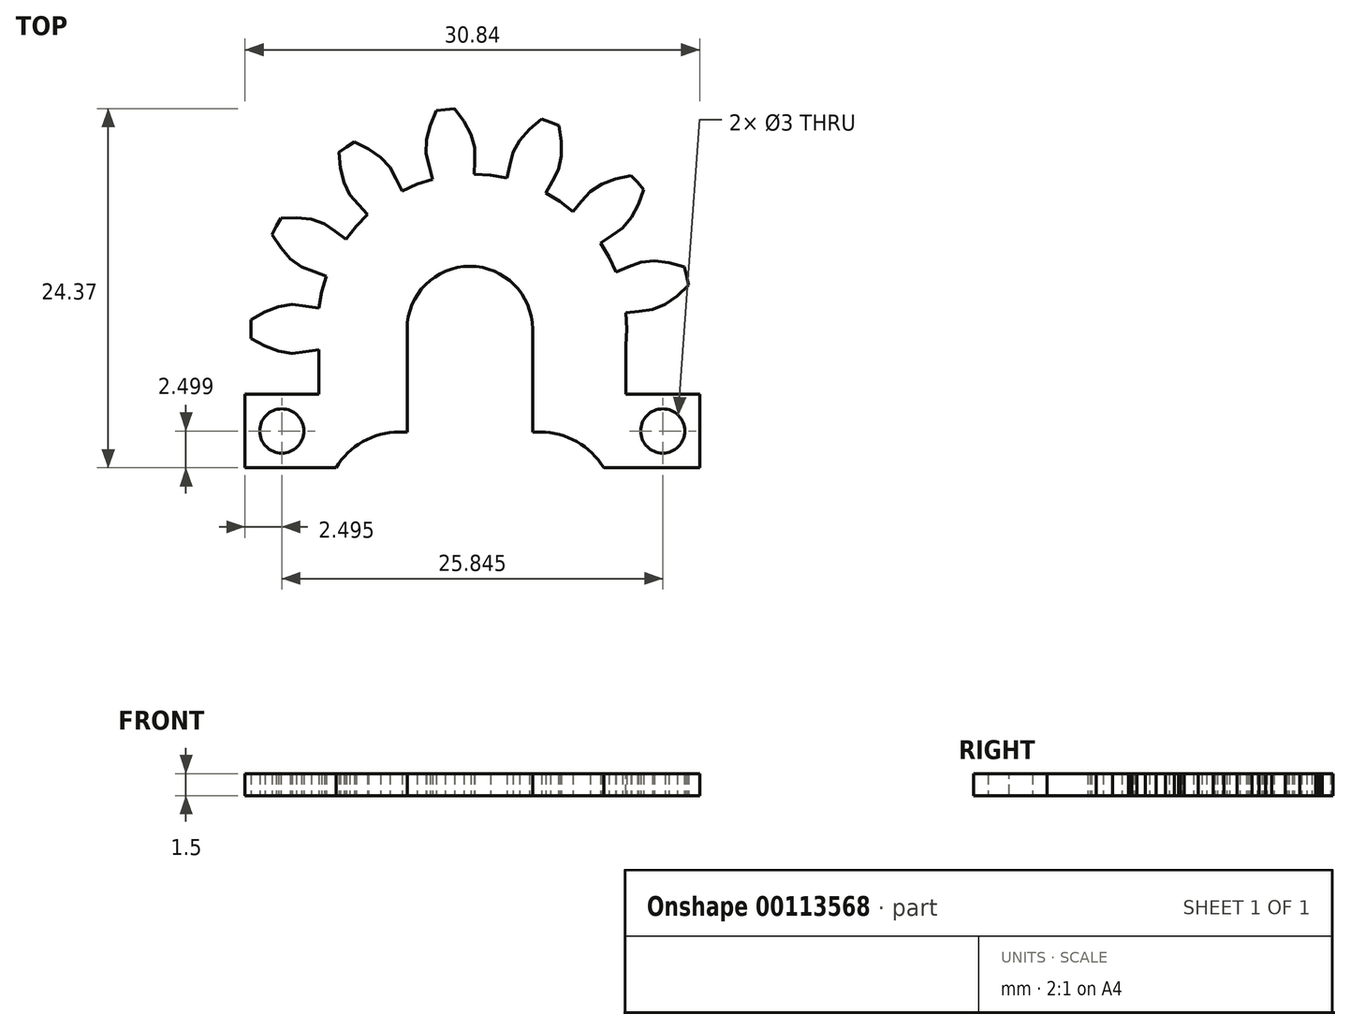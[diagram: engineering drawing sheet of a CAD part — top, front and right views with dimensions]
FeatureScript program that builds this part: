
annotation { "Feature Type Name" : "Feature", "Feature Type Description" : "" }
export const myFeature = defineFeature(function(context is Context, id is Id, definition is map)
    precondition{}
    {
        {
            var Q0;
            Q0=qCreatedBy(makeId("Top.planeOp"),FACE);
            var sketch = newSketch(context, id + "F0", { "sketchPlane" : qUnion([Q0])});
            skLineSegment(sketch, "E0", {"start": v(10.65, 0) * mm, "end": v(10.59, 1.11) * mm});
            skLineSegment(sketch, "E1", {"start": v(10.59, 1.11) * mm, "end": v(11.48, 1.2) * mm});
            skLineSegment(sketch, "E2", {"start": v(11.48, 1.2) * mm, "end": v(12.38, 1.3) * mm});
            skLineSegment(sketch, "E3", {"start": v(12.38, 1.3) * mm, "end": v(13.24, 1.67) * mm});
            skLineSegment(sketch, "E4", {"start": v(13.24, 1.67) * mm, "end": v(14.07, 2.24) * mm});
            skLineSegment(sketch, "E5", {"start": v(14.07, 2.24) * mm, "end": v(14.85, 2.97) * mm});
            skLineSegment(sketch, "E6", {"start": v(14.85, 2.97) * mm, "end": v(14.71, 3.59) * mm});
            skLineSegment(sketch, "E7", {"start": v(14.71, 3.59) * mm, "end": v(14.55, 4.2) * mm});
            skLineSegment(sketch, "E8", {"start": v(14.55, 4.2) * mm, "end": v(13.52, 4.49) * mm});
            skLineSegment(sketch, "E9", {"start": v(13.52, 4.49) * mm, "end": v(12.52, 4.6) * mm});
            skLineSegment(sketch, "E10", {"start": v(12.52, 4.6) * mm, "end": v(11.59, 4.53) * mm});
            skLineSegment(sketch, "E11", {"start": v(11.59, 4.53) * mm, "end": v(10.75, 4.2) * mm});
            skLineSegment(sketch, "E12", {"start": v(10.75, 4.2) * mm, "end": v(9.9, 3.87) * mm});
            skLineSegment(sketch, "E13", {"start": v(9.9, 3.87) * mm, "end": v(9.45, 4.88) * mm});
            skLineSegment(sketch, "E14", {"start": v(9.45, 4.88) * mm, "end": v(8.88, 5.84) * mm});
            skLineSegment(sketch, "E15", {"start": v(8.88, 5.84) * mm, "end": v(9.63, 6.34) * mm});
            skLineSegment(sketch, "E16", {"start": v(9.63, 6.34) * mm, "end": v(10.37, 6.84) * mm});
            skLineSegment(sketch, "E17", {"start": v(10.37, 6.84) * mm, "end": v(10.97, 7.56) * mm});
            skLineSegment(sketch, "E18", {"start": v(10.97, 7.56) * mm, "end": v(11.43, 8.45) * mm});
            skLineSegment(sketch, "E19", {"start": v(11.43, 8.45) * mm, "end": v(11.79, 9.46) * mm});
            skLineSegment(sketch, "E20", {"start": v(11.79, 9.46) * mm, "end": v(11.38, 9.95) * mm});
            skLineSegment(sketch, "E21", {"start": v(11.38, 9.95) * mm, "end": v(10.95, 10.41) * mm});
            skLineSegment(sketch, "E22", {"start": v(10.95, 10.41) * mm, "end": v(9.9, 10.19) * mm});
            skLineSegment(sketch, "E23", {"start": v(9.9, 10.19) * mm, "end": v(8.96, 9.83) * mm});
            skLineSegment(sketch, "E24", {"start": v(8.96, 9.83) * mm, "end": v(8.17, 9.32) * mm});
            skLineSegment(sketch, "E25", {"start": v(8.17, 9.32) * mm, "end": v(7.58, 8.64) * mm});
            skLineSegment(sketch, "E26", {"start": v(7.58, 8.64) * mm, "end": v(7, 7.96) * mm});
            skLineSegment(sketch, "E27", {"start": v(7, 7.96) * mm, "end": v(6.11, 8.64) * mm});
            skLineSegment(sketch, "E28", {"start": v(6.11, 8.64) * mm, "end": v(5.17, 9.22) * mm});
            skLineSegment(sketch, "E29", {"start": v(5.17, 9.22) * mm, "end": v(5.6, 10.01) * mm});
            skLineSegment(sketch, "E30", {"start": v(5.6, 10.01) * mm, "end": v(6.02, 10.8) * mm});
            skLineSegment(sketch, "E31", {"start": v(6.02, 10.8) * mm, "end": v(6.21, 11.72) * mm});
            skLineSegment(sketch, "E32", {"start": v(6.21, 11.72) * mm, "end": v(6.21, 12.73) * mm});
            skLineSegment(sketch, "E33", {"start": v(6.21, 12.73) * mm, "end": v(6.06, 13.79) * mm});
            skLineSegment(sketch, "E34", {"start": v(6.06, 13.79) * mm, "end": v(5.47, 14.03) * mm});
            skLineSegment(sketch, "E35", {"start": v(5.47, 14.03) * mm, "end": v(4.87, 14.24) * mm});
            skLineSegment(sketch, "E36", {"start": v(4.87, 14.24) * mm, "end": v(4.05, 13.55) * mm});
            skLineSegment(sketch, "E37", {"start": v(4.05, 13.55) * mm, "end": v(3.38, 12.8) * mm});
            skLineSegment(sketch, "E38", {"start": v(3.38, 12.8) * mm, "end": v(2.92, 11.98) * mm});
            skLineSegment(sketch, "E39", {"start": v(2.92, 11.98) * mm, "end": v(2.71, 11.1) * mm});
            skLineSegment(sketch, "E40", {"start": v(2.71, 11.1) * mm, "end": v(2.5, 10.23) * mm});
            skLineSegment(sketch, "E41", {"start": v(2.5, 10.23) * mm, "end": v(1.41, 10.42) * mm});
            skLineSegment(sketch, "E42", {"start": v(1.41, 10.42) * mm, "end": v(0.3, 10.5) * mm});
            skLineSegment(sketch, "E43", {"start": v(0.3, 10.5) * mm, "end": v(0.32, 11.4) * mm});
            skLineSegment(sketch, "E44", {"start": v(0.32, 11.4) * mm, "end": v(0.33, 12.3) * mm});
            skLineSegment(sketch, "E45", {"start": v(0.33, 12.3) * mm, "end": v(0.07, 13.2) * mm});
            skLineSegment(sketch, "E46", {"start": v(0.07, 13.2) * mm, "end": v(-0.4, 14.09) * mm});
            skLineSegment(sketch, "E47", {"start": v(-0.4, 14.09) * mm, "end": v(-1.03, 14.95) * mm});
            skLineSegment(sketch, "E48", {"start": v(-1.03, 14.95) * mm, "end": v(-1.66, 14.9) * mm});
            skLineSegment(sketch, "E49", {"start": v(-1.66, 14.9) * mm, "end": v(-2.29, 14.8) * mm});
            skLineSegment(sketch, "E50", {"start": v(-2.29, 14.8) * mm, "end": v(-2.7, 13.81) * mm});
            skLineSegment(sketch, "E51", {"start": v(-2.7, 13.81) * mm, "end": v(-2.93, 12.83) * mm});
            skLineSegment(sketch, "E52", {"start": v(-2.93, 12.83) * mm, "end": v(-2.97, 11.9) * mm});
            skLineSegment(sketch, "E53", {"start": v(-2.97, 11.9) * mm, "end": v(-2.74, 11.03) * mm});
            skLineSegment(sketch, "E54", {"start": v(-2.74, 11.03) * mm, "end": v(-2.52, 10.16) * mm});
            skLineSegment(sketch, "E55", {"start": v(-2.52, 10.16) * mm, "end": v(-3.57, 9.82) * mm});
            skLineSegment(sketch, "E56", {"start": v(-3.57, 9.82) * mm, "end": v(-4.6, 9.37) * mm});
            skLineSegment(sketch, "E57", {"start": v(-4.6, 9.37) * mm, "end": v(-5, 10.17) * mm});
            skLineSegment(sketch, "E58", {"start": v(-5, 10.17) * mm, "end": v(-5.41, 10.97) * mm});
            skLineSegment(sketch, "E59", {"start": v(-5.41, 10.97) * mm, "end": v(-6.05, 11.65) * mm});
            skLineSegment(sketch, "E60", {"start": v(-6.05, 11.65) * mm, "end": v(-6.88, 12.22) * mm});
            skLineSegment(sketch, "E61", {"start": v(-6.88, 12.22) * mm, "end": v(-7.84, 12.7) * mm});
            skLineSegment(sketch, "E62", {"start": v(-7.84, 12.7) * mm, "end": v(-8.37, 12.34) * mm});
            skLineSegment(sketch, "E63", {"start": v(-8.37, 12.34) * mm, "end": v(-8.89, 11.97) * mm});
            skLineSegment(sketch, "E64", {"start": v(-8.89, 11.97) * mm, "end": v(-8.79, 10.9) * mm});
            skLineSegment(sketch, "E65", {"start": v(-8.79, 10.9) * mm, "end": v(-8.55, 9.93) * mm});
            skLineSegment(sketch, "E66", {"start": v(-8.55, 9.93) * mm, "end": v(-8.14, 9.09) * mm});
            skLineSegment(sketch, "E67", {"start": v(-8.14, 9.09) * mm, "end": v(-7.54, 8.42) * mm});
            skLineSegment(sketch, "E68", {"start": v(-7.54, 8.42) * mm, "end": v(-6.93, 7.75) * mm});
            skLineSegment(sketch, "E69", {"start": v(-6.93, 7.75) * mm, "end": v(-7.71, 6.96) * mm});
            skLineSegment(sketch, "E70", {"start": v(-7.71, 6.96) * mm, "end": v(-8.4, 6.1) * mm});
            skLineSegment(sketch, "E71", {"start": v(-8.4, 6.1) * mm, "end": v(-9.14, 6.62) * mm});
            skLineSegment(sketch, "E72", {"start": v(-9.14, 6.62) * mm, "end": v(-9.87, 7.13) * mm});
            skLineSegment(sketch, "E73", {"start": v(-9.87, 7.13) * mm, "end": v(-10.76, 7.43) * mm});
            skLineSegment(sketch, "E74", {"start": v(-10.76, 7.43) * mm, "end": v(-11.76, 7.56) * mm});
            skLineSegment(sketch, "E75", {"start": v(-11.76, 7.56) * mm, "end": v(-12.83, 7.53) * mm});
            skLineSegment(sketch, "E76", {"start": v(-12.83, 7.53) * mm, "end": v(-13.13, 6.97) * mm});
            skLineSegment(sketch, "E77", {"start": v(-13.13, 6.97) * mm, "end": v(-13.42, 6.4) * mm});
            skLineSegment(sketch, "E78", {"start": v(-13.42, 6.4) * mm, "end": v(-12.83, 5.5) * mm});
            skLineSegment(sketch, "E79", {"start": v(-12.83, 5.5) * mm, "end": v(-12.17, 4.75) * mm});
            skLineSegment(sketch, "E80", {"start": v(-12.17, 4.75) * mm, "end": v(-11.41, 4.2) * mm});
            skLineSegment(sketch, "E81", {"start": v(-11.41, 4.2) * mm, "end": v(-10.57, 3.88) * mm});
            skLineSegment(sketch, "E82", {"start": v(-10.57, 3.88) * mm, "end": v(-9.72, 3.58) * mm});
            skLineSegment(sketch, "E83", {"start": v(-9.72, 3.58) * mm, "end": v(-10.05, 2.51) * mm});
            skLineSegment(sketch, "E84", {"start": v(-10.05, 2.51) * mm, "end": v(-10.25, 1.42) * mm});
            skLineSegment(sketch, "E85", {"start": v(-10.25, 1.42) * mm, "end": v(-11.15, 1.54) * mm});
            skLineSegment(sketch, "E86", {"start": v(-11.15, 1.54) * mm, "end": v(-12.04, 1.66) * mm});
            skLineSegment(sketch, "E87", {"start": v(-12.04, 1.66) * mm, "end": v(-12.96, 1.51) * mm});
            skLineSegment(sketch, "E88", {"start": v(-12.96, 1.51) * mm, "end": v(-13.9, 1.16) * mm});
            skLineSegment(sketch, "E89", {"start": v(-13.9, 1.16) * mm, "end": v(-14.84, 0.63) * mm});
            skLineSegment(sketch, "E90", {"start": v(-14.84, 0.63) * mm, "end": v(-14.85, 0) * mm});
            skLineSegment(sketch, "E91", {"start": v(-14.85, 0) * mm, "end": v(-14.84, -0.63) * mm});
            skLineSegment(sketch, "E92", {"start": v(-14.84, -0.63) * mm, "end": v(-13.9, -1.16) * mm});
            skLineSegment(sketch, "E93", {"start": v(-13.9, -1.16) * mm, "end": v(-12.96, -1.51) * mm});
            skLineSegment(sketch, "E94", {"start": v(-12.96, -1.51) * mm, "end": v(-12.04, -1.66) * mm});
            skLineSegment(sketch, "E95", {"start": v(-12.04, -1.66) * mm, "end": v(-11.15, -1.54) * mm});
            skLineSegment(sketch, "E96", {"start": v(-11.15, -1.54) * mm, "end": v(-10.25, -1.42) * mm});
            skLineSegment(sketch, "E97", {"start": v(-10.25, -1.42) * mm, "end": v(-10.05, -2.51) * mm});
            skLineSegment(sketch, "E98", {"start": v(-10.05, -2.51) * mm, "end": v(-9.72, -3.58) * mm});
            skLineSegment(sketch, "E99", {"start": v(-9.72, -3.58) * mm, "end": v(-10.57, -3.88) * mm});
            skLineSegment(sketch, "E100", {"start": v(-10.57, -3.88) * mm, "end": v(-11.41, -4.2) * mm});
            skLineSegment(sketch, "E101", {"start": v(-11.41, -4.2) * mm, "end": v(-12.17, -4.75) * mm});
            skLineSegment(sketch, "E102", {"start": v(-12.17, -4.75) * mm, "end": v(-12.83, -5.5) * mm});
            skLineSegment(sketch, "E103", {"start": v(-12.83, -5.5) * mm, "end": v(-13.42, -6.4) * mm});
            skLineSegment(sketch, "E104", {"start": v(-13.42, -6.4) * mm, "end": v(-13.13, -6.97) * mm});
            skLineSegment(sketch, "E105", {"start": v(-13.13, -6.97) * mm, "end": v(-12.83, -7.53) * mm});
            skLineSegment(sketch, "E106", {"start": v(-12.83, -7.53) * mm, "end": v(-11.76, -7.56) * mm});
            skLineSegment(sketch, "E107", {"start": v(-11.76, -7.56) * mm, "end": v(-10.76, -7.43) * mm});
            skLineSegment(sketch, "E108", {"start": v(-10.76, -7.43) * mm, "end": v(-9.87, -7.13) * mm});
            skLineSegment(sketch, "E109", {"start": v(-9.87, -7.13) * mm, "end": v(-9.14, -6.62) * mm});
            skLineSegment(sketch, "E110", {"start": v(-9.14, -6.62) * mm, "end": v(-8.4, -6.1) * mm});
            skLineSegment(sketch, "E111", {"start": v(-8.4, -6.1) * mm, "end": v(-7.71, -6.96) * mm});
            skLineSegment(sketch, "E112", {"start": v(-7.71, -6.96) * mm, "end": v(-6.93, -7.75) * mm});
            skLineSegment(sketch, "E113", {"start": v(-6.93, -7.75) * mm, "end": v(-7.54, -8.42) * mm});
            skLineSegment(sketch, "E114", {"start": v(-7.54, -8.42) * mm, "end": v(-8.14, -9.09) * mm});
            skLineSegment(sketch, "E115", {"start": v(-8.14, -9.09) * mm, "end": v(-8.55, -9.93) * mm});
            skLineSegment(sketch, "E116", {"start": v(-8.55, -9.93) * mm, "end": v(-8.79, -10.9) * mm});
            skLineSegment(sketch, "E117", {"start": v(-8.79, -10.9) * mm, "end": v(-8.89, -11.97) * mm});
            skLineSegment(sketch, "E118", {"start": v(-8.89, -11.97) * mm, "end": v(-8.37, -12.34) * mm});
            skLineSegment(sketch, "E119", {"start": v(-8.37, -12.34) * mm, "end": v(-7.84, -12.7) * mm});
            skLineSegment(sketch, "E120", {"start": v(-7.84, -12.7) * mm, "end": v(-6.88, -12.22) * mm});
            skLineSegment(sketch, "E121", {"start": v(-6.88, -12.22) * mm, "end": v(-6.05, -11.65) * mm});
            skLineSegment(sketch, "E122", {"start": v(-6.05, -11.65) * mm, "end": v(-5.41, -10.97) * mm});
            skLineSegment(sketch, "E123", {"start": v(-5.41, -10.97) * mm, "end": v(-5, -10.17) * mm});
            skLineSegment(sketch, "E124", {"start": v(-5, -10.17) * mm, "end": v(-4.6, -9.37) * mm});
            skLineSegment(sketch, "E125", {"start": v(-4.6, -9.37) * mm, "end": v(-3.57, -9.82) * mm});
            skLineSegment(sketch, "E126", {"start": v(-3.57, -9.82) * mm, "end": v(-2.52, -10.16) * mm});
            skLineSegment(sketch, "E127", {"start": v(-2.52, -10.16) * mm, "end": v(-2.74, -11.03) * mm});
            skLineSegment(sketch, "E128", {"start": v(-2.74, -11.03) * mm, "end": v(-2.97, -11.9) * mm});
            skLineSegment(sketch, "E129", {"start": v(-2.97, -11.9) * mm, "end": v(-2.93, -12.83) * mm});
            skLineSegment(sketch, "E130", {"start": v(-2.93, -12.83) * mm, "end": v(-2.7, -13.81) * mm});
            skLineSegment(sketch, "E131", {"start": v(-2.7, -13.81) * mm, "end": v(-2.29, -14.8) * mm});
            skLineSegment(sketch, "E132", {"start": v(-2.29, -14.8) * mm, "end": v(-1.66, -14.9) * mm});
            skLineSegment(sketch, "E133", {"start": v(-1.66, -14.9) * mm, "end": v(-1.03, -14.95) * mm});
            skLineSegment(sketch, "E134", {"start": v(-1.03, -14.95) * mm, "end": v(-0.4, -14.09) * mm});
            skLineSegment(sketch, "E135", {"start": v(-0.4, -14.09) * mm, "end": v(0.07, -13.2) * mm});
            skLineSegment(sketch, "E136", {"start": v(0.07, -13.2) * mm, "end": v(0.33, -12.3) * mm});
            skLineSegment(sketch, "E137", {"start": v(0.33, -12.3) * mm, "end": v(0.32, -11.4) * mm});
            skLineSegment(sketch, "E138", {"start": v(0.32, -11.4) * mm, "end": v(0.3, -10.5) * mm});
            skLineSegment(sketch, "E139", {"start": v(0.3, -10.5) * mm, "end": v(1.41, -10.42) * mm});
            skLineSegment(sketch, "E140", {"start": v(1.41, -10.42) * mm, "end": v(2.5, -10.23) * mm});
            skLineSegment(sketch, "E141", {"start": v(2.5, -10.23) * mm, "end": v(2.71, -11.1) * mm});
            skLineSegment(sketch, "E142", {"start": v(2.71, -11.1) * mm, "end": v(2.92, -11.98) * mm});
            skLineSegment(sketch, "E143", {"start": v(2.92, -11.98) * mm, "end": v(3.38, -12.8) * mm});
            skLineSegment(sketch, "E144", {"start": v(3.38, -12.8) * mm, "end": v(4.05, -13.55) * mm});
            skLineSegment(sketch, "E145", {"start": v(4.05, -13.55) * mm, "end": v(4.87, -14.24) * mm});
            skLineSegment(sketch, "E146", {"start": v(4.87, -14.24) * mm, "end": v(5.47, -14.03) * mm});
            skLineSegment(sketch, "E147", {"start": v(5.47, -14.03) * mm, "end": v(6.06, -13.79) * mm});
            skLineSegment(sketch, "E148", {"start": v(6.06, -13.79) * mm, "end": v(6.21, -12.73) * mm});
            skLineSegment(sketch, "E149", {"start": v(6.21, -12.73) * mm, "end": v(6.21, -11.72) * mm});
            skLineSegment(sketch, "E150", {"start": v(6.21, -11.72) * mm, "end": v(6.02, -10.8) * mm});
            skLineSegment(sketch, "E151", {"start": v(6.02, -10.8) * mm, "end": v(5.6, -10.01) * mm});
            skLineSegment(sketch, "E152", {"start": v(5.6, -10.01) * mm, "end": v(5.17, -9.22) * mm});
            skLineSegment(sketch, "E153", {"start": v(5.17, -9.22) * mm, "end": v(6.11, -8.64) * mm});
            skLineSegment(sketch, "E154", {"start": v(6.11, -8.64) * mm, "end": v(7, -7.96) * mm});
            skLineSegment(sketch, "E155", {"start": v(7, -7.96) * mm, "end": v(7.58, -8.64) * mm});
            skLineSegment(sketch, "E156", {"start": v(7.58, -8.64) * mm, "end": v(8.17, -9.32) * mm});
            skLineSegment(sketch, "E157", {"start": v(8.17, -9.32) * mm, "end": v(8.96, -9.83) * mm});
            skLineSegment(sketch, "E158", {"start": v(8.96, -9.83) * mm, "end": v(9.9, -10.19) * mm});
            skLineSegment(sketch, "E159", {"start": v(9.9, -10.19) * mm, "end": v(10.95, -10.41) * mm});
            skLineSegment(sketch, "E160", {"start": v(10.95, -10.41) * mm, "end": v(11.38, -9.95) * mm});
            skLineSegment(sketch, "E161", {"start": v(11.38, -9.95) * mm, "end": v(11.79, -9.46) * mm});
            skLineSegment(sketch, "E162", {"start": v(11.79, -9.46) * mm, "end": v(11.43, -8.45) * mm});
            skLineSegment(sketch, "E163", {"start": v(11.43, -8.45) * mm, "end": v(10.97, -7.56) * mm});
            skLineSegment(sketch, "E164", {"start": v(10.97, -7.56) * mm, "end": v(10.37, -6.84) * mm});
            skLineSegment(sketch, "E165", {"start": v(10.37, -6.84) * mm, "end": v(9.63, -6.34) * mm});
            skLineSegment(sketch, "E166", {"start": v(9.63, -6.34) * mm, "end": v(8.88, -5.84) * mm});
            skLineSegment(sketch, "E167", {"start": v(8.88, -5.84) * mm, "end": v(9.45, -4.88) * mm});
            skLineSegment(sketch, "E168", {"start": v(9.45, -4.88) * mm, "end": v(9.9, -3.87) * mm});
            skLineSegment(sketch, "E169", {"start": v(9.9, -3.87) * mm, "end": v(10.75, -4.2) * mm});
            skLineSegment(sketch, "E170", {"start": v(10.75, -4.2) * mm, "end": v(11.59, -4.53) * mm});
            skLineSegment(sketch, "E171", {"start": v(11.59, -4.53) * mm, "end": v(12.52, -4.6) * mm});
            skLineSegment(sketch, "E172", {"start": v(12.52, -4.6) * mm, "end": v(13.52, -4.49) * mm});
            skLineSegment(sketch, "E173", {"start": v(13.52, -4.49) * mm, "end": v(14.55, -4.2) * mm});
            skLineSegment(sketch, "E174", {"start": v(14.55, -4.2) * mm, "end": v(14.71, -3.59) * mm});
            skLineSegment(sketch, "E175", {"start": v(14.71, -3.59) * mm, "end": v(14.85, -2.97) * mm});
            skLineSegment(sketch, "E176", {"start": v(14.85, -2.97) * mm, "end": v(14.07, -2.24) * mm});
            skLineSegment(sketch, "E177", {"start": v(14.07, -2.24) * mm, "end": v(13.24, -1.67) * mm});
            skLineSegment(sketch, "E178", {"start": v(13.24, -1.67) * mm, "end": v(12.38, -1.3) * mm});
            skLineSegment(sketch, "E179", {"start": v(12.38, -1.3) * mm, "end": v(11.48, -1.2) * mm});
            skLineSegment(sketch, "E180", {"start": v(11.48, -1.2) * mm, "end": v(10.59, -1.11) * mm});
            skLineSegment(sketch, "E181", {"start": v(10.65, 0) * mm, "end": v(10.59, -1.11) * mm});
            skSolve(sketch);
        }
        {
            var Q0;
            Q0 = qSketchRegion(id + "F0", true);
            extrude(context, id + "F1", {"entities" : qUnion([Q0]), "depth" : 1.5 * mm});
        }
        {
            var Q0;
            Q0=makeQuery(id+"F1.opExtrude","CAP_FACE",FACE,{"disambiguationData":[OSD([sQuery(id+"F0.wireOp",EDGE,"E0"),sQuery(id+"F0.wireOp",EDGE,"E1"),sQuery(id+"F0.wireOp",EDGE,"E2"),sQuery(id+"F0.wireOp",EDGE,"E3"),sQuery(id+"F0.wireOp",EDGE,"E4"),sQuery(id+"F0.wireOp",EDGE,"E5"),sQuery(id+"F0.wireOp",EDGE,"E6"),sQuery(id+"F0.wireOp",EDGE,"E7"),sQuery(id+"F0.wireOp",EDGE,"E8"),sQuery(id+"F0.wireOp",EDGE,"E9"),sQuery(id+"F0.wireOp",EDGE,"E10"),sQuery(id+"F0.wireOp",EDGE,"E11"),sQuery(id+"F0.wireOp",EDGE,"E12"),sQuery(id+"F0.wireOp",EDGE,"E13"),sQuery(id+"F0.wireOp",EDGE,"E14"),sQuery(id+"F0.wireOp",EDGE,"E15"),sQuery(id+"F0.wireOp",EDGE,"E16"),sQuery(id+"F0.wireOp",EDGE,"E17"),sQuery(id+"F0.wireOp",EDGE,"E18"),sQuery(id+"F0.wireOp",EDGE,"E19"),sQuery(id+"F0.wireOp",EDGE,"E20"),sQuery(id+"F0.wireOp",EDGE,"E21"),sQuery(id+"F0.wireOp",EDGE,"E22"),sQuery(id+"F0.wireOp",EDGE,"E23"),sQuery(id+"F0.wireOp",EDGE,"E24"),sQuery(id+"F0.wireOp",EDGE,"E25"),sQuery(id+"F0.wireOp",EDGE,"E26"),sQuery(id+"F0.wireOp",EDGE,"E27"),sQuery(id+"F0.wireOp",EDGE,"E28"),sQuery(id+"F0.wireOp",EDGE,"E29"),sQuery(id+"F0.wireOp",EDGE,"E30"),sQuery(id+"F0.wireOp",EDGE,"E31"),sQuery(id+"F0.wireOp",EDGE,"E32"),sQuery(id+"F0.wireOp",EDGE,"E33"),sQuery(id+"F0.wireOp",EDGE,"E34"),sQuery(id+"F0.wireOp",EDGE,"E35"),sQuery(id+"F0.wireOp",EDGE,"E36"),sQuery(id+"F0.wireOp",EDGE,"E37"),sQuery(id+"F0.wireOp",EDGE,"E38"),sQuery(id+"F0.wireOp",EDGE,"E39"),sQuery(id+"F0.wireOp",EDGE,"E40"),sQuery(id+"F0.wireOp",EDGE,"E41"),sQuery(id+"F0.wireOp",EDGE,"E42"),sQuery(id+"F0.wireOp",EDGE,"E43"),sQuery(id+"F0.wireOp",EDGE,"E44"),sQuery(id+"F0.wireOp",EDGE,"E45"),sQuery(id+"F0.wireOp",EDGE,"E46"),sQuery(id+"F0.wireOp",EDGE,"E47"),sQuery(id+"F0.wireOp",EDGE,"E48"),sQuery(id+"F0.wireOp",EDGE,"E49"),sQuery(id+"F0.wireOp",EDGE,"E50"),sQuery(id+"F0.wireOp",EDGE,"E51"),sQuery(id+"F0.wireOp",EDGE,"E52"),sQuery(id+"F0.wireOp",EDGE,"E53"),sQuery(id+"F0.wireOp",EDGE,"E54"),sQuery(id+"F0.wireOp",EDGE,"E55"),sQuery(id+"F0.wireOp",EDGE,"E56"),sQuery(id+"F0.wireOp",EDGE,"E57"),sQuery(id+"F0.wireOp",EDGE,"E58"),sQuery(id+"F0.wireOp",EDGE,"E59"),sQuery(id+"F0.wireOp",EDGE,"E60"),sQuery(id+"F0.wireOp",EDGE,"E61"),sQuery(id+"F0.wireOp",EDGE,"E62"),sQuery(id+"F0.wireOp",EDGE,"E63"),sQuery(id+"F0.wireOp",EDGE,"E64"),sQuery(id+"F0.wireOp",EDGE,"E65"),sQuery(id+"F0.wireOp",EDGE,"E66"),sQuery(id+"F0.wireOp",EDGE,"E67"),sQuery(id+"F0.wireOp",EDGE,"E68"),sQuery(id+"F0.wireOp",EDGE,"E69"),sQuery(id+"F0.wireOp",EDGE,"E70"),sQuery(id+"F0.wireOp",EDGE,"E71"),sQuery(id+"F0.wireOp",EDGE,"E72"),sQuery(id+"F0.wireOp",EDGE,"E73"),sQuery(id+"F0.wireOp",EDGE,"E74"),sQuery(id+"F0.wireOp",EDGE,"E75"),sQuery(id+"F0.wireOp",EDGE,"E76"),sQuery(id+"F0.wireOp",EDGE,"E77"),sQuery(id+"F0.wireOp",EDGE,"E78"),sQuery(id+"F0.wireOp",EDGE,"E79"),sQuery(id+"F0.wireOp",EDGE,"E80"),sQuery(id+"F0.wireOp",EDGE,"E81"),sQuery(id+"F0.wireOp",EDGE,"E82"),sQuery(id+"F0.wireOp",EDGE,"E83"),sQuery(id+"F0.wireOp",EDGE,"E84"),sQuery(id+"F0.wireOp",EDGE,"E85"),sQuery(id+"F0.wireOp",EDGE,"E86"),sQuery(id+"F0.wireOp",EDGE,"E87"),sQuery(id+"F0.wireOp",EDGE,"E88"),sQuery(id+"F0.wireOp",EDGE,"E89"),sQuery(id+"F0.wireOp",EDGE,"E90"),sQuery(id+"F0.wireOp",EDGE,"E91"),sQuery(id+"F0.wireOp",EDGE,"E92"),sQuery(id+"F0.wireOp",EDGE,"E93"),sQuery(id+"F0.wireOp",EDGE,"E94"),sQuery(id+"F0.wireOp",EDGE,"E95"),sQuery(id+"F0.wireOp",EDGE,"E96"),sQuery(id+"F0.wireOp",EDGE,"E97"),sQuery(id+"F0.wireOp",EDGE,"E98"),sQuery(id+"F0.wireOp",EDGE,"E99"),sQuery(id+"F0.wireOp",EDGE,"E100"),sQuery(id+"F0.wireOp",EDGE,"E101"),sQuery(id+"F0.wireOp",EDGE,"E102"),sQuery(id+"F0.wireOp",EDGE,"E103"),sQuery(id+"F0.wireOp",EDGE,"E104"),sQuery(id+"F0.wireOp",EDGE,"E105"),sQuery(id+"F0.wireOp",EDGE,"E106"),sQuery(id+"F0.wireOp",EDGE,"E107"),sQuery(id+"F0.wireOp",EDGE,"E108"),sQuery(id+"F0.wireOp",EDGE,"E109"),sQuery(id+"F0.wireOp",EDGE,"E110"),sQuery(id+"F0.wireOp",EDGE,"E111"),sQuery(id+"F0.wireOp",EDGE,"E112"),sQuery(id+"F0.wireOp",EDGE,"E113"),sQuery(id+"F0.wireOp",EDGE,"E114"),sQuery(id+"F0.wireOp",EDGE,"E115"),sQuery(id+"F0.wireOp",EDGE,"E116"),sQuery(id+"F0.wireOp",EDGE,"E117"),sQuery(id+"F0.wireOp",EDGE,"E118"),sQuery(id+"F0.wireOp",EDGE,"E119"),sQuery(id+"F0.wireOp",EDGE,"E120"),sQuery(id+"F0.wireOp",EDGE,"E121"),sQuery(id+"F0.wireOp",EDGE,"E122"),sQuery(id+"F0.wireOp",EDGE,"E123"),sQuery(id+"F0.wireOp",EDGE,"E124"),sQuery(id+"F0.wireOp",EDGE,"E125"),sQuery(id+"F0.wireOp",EDGE,"E126"),sQuery(id+"F0.wireOp",EDGE,"E127"),sQuery(id+"F0.wireOp",EDGE,"E128"),sQuery(id+"F0.wireOp",EDGE,"E129"),sQuery(id+"F0.wireOp",EDGE,"E130"),sQuery(id+"F0.wireOp",EDGE,"E131"),sQuery(id+"F0.wireOp",EDGE,"E132"),sQuery(id+"F0.wireOp",EDGE,"E133"),sQuery(id+"F0.wireOp",EDGE,"E134"),sQuery(id+"F0.wireOp",EDGE,"E135"),sQuery(id+"F0.wireOp",EDGE,"E136"),sQuery(id+"F0.wireOp",EDGE,"E137"),sQuery(id+"F0.wireOp",EDGE,"E138"),sQuery(id+"F0.wireOp",EDGE,"E139"),sQuery(id+"F0.wireOp",EDGE,"E140"),sQuery(id+"F0.wireOp",EDGE,"E141"),sQuery(id+"F0.wireOp",EDGE,"E142"),sQuery(id+"F0.wireOp",EDGE,"E143"),sQuery(id+"F0.wireOp",EDGE,"E144"),sQuery(id+"F0.wireOp",EDGE,"E145"),sQuery(id+"F0.wireOp",EDGE,"E146"),sQuery(id+"F0.wireOp",EDGE,"E147"),sQuery(id+"F0.wireOp",EDGE,"E148"),sQuery(id+"F0.wireOp",EDGE,"E149"),sQuery(id+"F0.wireOp",EDGE,"E150"),sQuery(id+"F0.wireOp",EDGE,"E151"),sQuery(id+"F0.wireOp",EDGE,"E152"),sQuery(id+"F0.wireOp",EDGE,"E153"),sQuery(id+"F0.wireOp",EDGE,"E154"),sQuery(id+"F0.wireOp",EDGE,"E155"),sQuery(id+"F0.wireOp",EDGE,"E156"),sQuery(id+"F0.wireOp",EDGE,"E157"),sQuery(id+"F0.wireOp",EDGE,"E158"),sQuery(id+"F0.wireOp",EDGE,"E159"),sQuery(id+"F0.wireOp",EDGE,"E160"),sQuery(id+"F0.wireOp",EDGE,"E161"),sQuery(id+"F0.wireOp",EDGE,"E162"),sQuery(id+"F0.wireOp",EDGE,"E163"),sQuery(id+"F0.wireOp",EDGE,"E164"),sQuery(id+"F0.wireOp",EDGE,"E165"),sQuery(id+"F0.wireOp",EDGE,"E166"),sQuery(id+"F0.wireOp",EDGE,"E167"),sQuery(id+"F0.wireOp",EDGE,"E168"),sQuery(id+"F0.wireOp",EDGE,"E169"),sQuery(id+"F0.wireOp",EDGE,"E170"),sQuery(id+"F0.wireOp",EDGE,"E171"),sQuery(id+"F0.wireOp",EDGE,"E172"),sQuery(id+"F0.wireOp",EDGE,"E173"),sQuery(id+"F0.wireOp",EDGE,"E174"),sQuery(id+"F0.wireOp",EDGE,"E175"),sQuery(id+"F0.wireOp",EDGE,"E176"),sQuery(id+"F0.wireOp",EDGE,"E177"),sQuery(id+"F0.wireOp",EDGE,"E178"),sQuery(id+"F0.wireOp",EDGE,"E179"),sQuery(id+"F0.wireOp",EDGE,"E180"),sQuery(id+"F0.wireOp",EDGE,"E181")])],"isStart":false});
            var sketch = newSketch(context, id + "F2", { "sketchPlane" : qUnion([Q0])});
            skArc(sketch, "E182", {"start": v(4.25, 0) * mm, "mid": v(0, 4.25) * mm, "end": v(-4.25, 0) * mm});
            skLineSegment(sketch, "E183", {"start": v(-10.25, -1.42) * mm, "end": v(-4.25, -1.42) * mm});
            skLineSegment(sketch, "E184.0", {"start": v(10.65, 0) * mm, "end": v(10.59, -1.11) * mm});
            skLineSegment(sketch, "E185", {"start": v(10.59, -1.11) * mm, "end": v(10.59, -1.42) * mm});
            skLineSegment(sketch, "E186", {"start": v(-4.25, 0) * mm, "end": v(-4.25, -1.42) * mm});
            skLineSegment(sketch, "E187.MirrorCS", {"start": v(4.25, 0) * mm, "end": v(4.25, -1.42) * mm});
            skLineSegment(sketch, "E188.trimOffspring", {"start": v(4.25, -1.42) * mm, "end": v(10.59, -1.42) * mm});
            skSolve(sketch);
        }
        {
            var Q0;
            Q0=makeQuery(id+"F2.imprint","IMPRINT",FACE,{"disambiguationData":[TD([[makeQuery(id+"F2.imprint","IMPRINT",EDGE,{"derivedFrom":sQuery(id+"F2.wireOp",EDGE,"E182")}),1.0]])]});
            extrude(context, id + "F3", {"entities" : qUnion([Q0]), "operationType" : NewBodyOperationType.REMOVE, "endBound" : BoundingType.UP_TO_NEXT, "oppositeDirection" : true, "depth" : 25 * mm});
        }
        {
            var Q0;
            Q0=makeQuery(id+"F3.boolean.opBoolean","COPY",FACE,{"derivedFrom":makeQuery(id+"F3.opExtrude","SWEPT_FACE",FACE,{"disambiguationData":[OSD([sQuery(id+"F2.wireOp",EDGE,"E183")])]})});
            var sketch = newSketch(context, id + "F4", { "sketchPlane" : qUnion([Q0])});
            skLineSegment(sketch, "E189.bottom", {"start": v(-10.25, 1.5) * mm, "end": v(-4.25, 1.5) * mm});
            skLineSegment(sketch, "E189.top", {"start": v(-10.25, 0) * mm, "end": v(-4.25, 0) * mm});
            skLineSegment(sketch, "E189.left", {"start": v(-10.25, 1.5) * mm, "end": v(-10.25, 0) * mm});
            skLineSegment(sketch, "E189.right", {"start": v(-4.25, 1.5) * mm, "end": v(-4.25, 0) * mm});
            skLineSegment(sketch, "E190.0", {"start": v(4.25, 1.5) * mm, "end": v(10.59, 1.5) * mm});
            skLineSegment(sketch, "E191.0", {"start": v(4.25, 0) * mm, "end": v(4.25, 1.5) * mm});
            skLineSegment(sketch, "E192.0.0", {"start": v(10.59, 0) * mm, "end": v(10.59, 1.5) * mm});
            skLineSegment(sketch, "E192.0.1", {"start": v(10.59, 1.5) * mm, "end": v(4.25, 1.5) * mm});
            skLineSegment(sketch, "E192.0.2", {"start": v(4.25, 1.5) * mm, "end": v(4.25, 0) * mm});
            skLineSegment(sketch, "E192.0.3", {"start": v(4.25, 0) * mm, "end": v(10.59, 0) * mm});
            skSolve(sketch);
        }
        {
            var Q0;
            Q0 = qSketchRegion(id + "F4", true);
            extrude(context, id + "F5", {"entities" : qUnion([Q0]), "operationType" : NewBodyOperationType.ADD, "depth" : 8 * mm});
        }
        {
            var Q0;
            Q0=makeQuery(id+"F5.boolean.opBoolean","MERGE",FACE,{"derivedFrom":[makeQuery(id+"F3.boolean.opBoolean","COPY",FACE,{"derivedFrom":makeQuery(id+"F3.opExtrude","SWEPT_FACE",FACE,{"disambiguationData":[OSD([sQuery(id+"F2.wireOp",EDGE,"E185")])]})}),makeQuery(id+"F5.opExtrude","SWEPT_FACE",FACE,{"disambiguationData":[OSD([sQuery(id+"F4.wireOp",EDGE,"E192.0.0")])]})]});
            var sketch = newSketch(context, id + "F6", { "sketchPlane" : qUnion([Q0])});
            skLineSegment(sketch, "E193.bottom", {"start": v(-9.42, 0) * mm, "end": v(-4.42, 0) * mm});
            skLineSegment(sketch, "E193.top", {"start": v(-9.42, 1.5) * mm, "end": v(-4.42, 1.5) * mm});
            skLineSegment(sketch, "E193.left", {"start": v(-9.42, 0) * mm, "end": v(-9.42, 1.5) * mm});
            skLineSegment(sketch, "E193.right", {"start": v(-4.42, 0) * mm, "end": v(-4.42, 1.5) * mm});
            skSolve(sketch);
        }
        {
            var Q0;
            Q0 = qSketchRegion(id + "F6", true);
            extrude(context, id + "F7", {"entities" : qUnion([Q0]), "operationType" : NewBodyOperationType.ADD, "depth" : 5 * mm});
        }
        {
            var Q0;
            Q0=makeQuery(id+"F7.boolean.opBoolean","MERGE",FACE,{"derivedFrom":[makeQuery(id+"F5.boolean.opBoolean","MERGE",FACE,{"derivedFrom":[makeQuery(id+"F1.opExtrude","CAP_FACE",FACE,{"disambiguationData":[OSD([sQuery(id+"F0.wireOp",EDGE,"E0"),sQuery(id+"F0.wireOp",EDGE,"E1"),sQuery(id+"F0.wireOp",EDGE,"E2"),sQuery(id+"F0.wireOp",EDGE,"E3"),sQuery(id+"F0.wireOp",EDGE,"E4"),sQuery(id+"F0.wireOp",EDGE,"E5"),sQuery(id+"F0.wireOp",EDGE,"E6"),sQuery(id+"F0.wireOp",EDGE,"E7"),sQuery(id+"F0.wireOp",EDGE,"E8"),sQuery(id+"F0.wireOp",EDGE,"E9"),sQuery(id+"F0.wireOp",EDGE,"E10"),sQuery(id+"F0.wireOp",EDGE,"E11"),sQuery(id+"F0.wireOp",EDGE,"E12"),sQuery(id+"F0.wireOp",EDGE,"E13"),sQuery(id+"F0.wireOp",EDGE,"E14"),sQuery(id+"F0.wireOp",EDGE,"E15"),sQuery(id+"F0.wireOp",EDGE,"E16"),sQuery(id+"F0.wireOp",EDGE,"E17"),sQuery(id+"F0.wireOp",EDGE,"E18"),sQuery(id+"F0.wireOp",EDGE,"E19"),sQuery(id+"F0.wireOp",EDGE,"E20"),sQuery(id+"F0.wireOp",EDGE,"E21"),sQuery(id+"F0.wireOp",EDGE,"E22"),sQuery(id+"F0.wireOp",EDGE,"E23"),sQuery(id+"F0.wireOp",EDGE,"E24"),sQuery(id+"F0.wireOp",EDGE,"E25"),sQuery(id+"F0.wireOp",EDGE,"E26"),sQuery(id+"F0.wireOp",EDGE,"E27"),sQuery(id+"F0.wireOp",EDGE,"E28"),sQuery(id+"F0.wireOp",EDGE,"E29"),sQuery(id+"F0.wireOp",EDGE,"E30"),sQuery(id+"F0.wireOp",EDGE,"E31"),sQuery(id+"F0.wireOp",EDGE,"E32"),sQuery(id+"F0.wireOp",EDGE,"E33"),sQuery(id+"F0.wireOp",EDGE,"E34"),sQuery(id+"F0.wireOp",EDGE,"E35"),sQuery(id+"F0.wireOp",EDGE,"E36"),sQuery(id+"F0.wireOp",EDGE,"E37"),sQuery(id+"F0.wireOp",EDGE,"E38"),sQuery(id+"F0.wireOp",EDGE,"E39"),sQuery(id+"F0.wireOp",EDGE,"E40"),sQuery(id+"F0.wireOp",EDGE,"E41"),sQuery(id+"F0.wireOp",EDGE,"E42"),sQuery(id+"F0.wireOp",EDGE,"E43"),sQuery(id+"F0.wireOp",EDGE,"E44"),sQuery(id+"F0.wireOp",EDGE,"E45"),sQuery(id+"F0.wireOp",EDGE,"E46"),sQuery(id+"F0.wireOp",EDGE,"E47"),sQuery(id+"F0.wireOp",EDGE,"E48"),sQuery(id+"F0.wireOp",EDGE,"E49"),sQuery(id+"F0.wireOp",EDGE,"E50"),sQuery(id+"F0.wireOp",EDGE,"E51"),sQuery(id+"F0.wireOp",EDGE,"E52"),sQuery(id+"F0.wireOp",EDGE,"E53"),sQuery(id+"F0.wireOp",EDGE,"E54"),sQuery(id+"F0.wireOp",EDGE,"E55"),sQuery(id+"F0.wireOp",EDGE,"E56"),sQuery(id+"F0.wireOp",EDGE,"E57"),sQuery(id+"F0.wireOp",EDGE,"E58"),sQuery(id+"F0.wireOp",EDGE,"E59"),sQuery(id+"F0.wireOp",EDGE,"E60"),sQuery(id+"F0.wireOp",EDGE,"E61"),sQuery(id+"F0.wireOp",EDGE,"E62"),sQuery(id+"F0.wireOp",EDGE,"E63"),sQuery(id+"F0.wireOp",EDGE,"E64"),sQuery(id+"F0.wireOp",EDGE,"E65"),sQuery(id+"F0.wireOp",EDGE,"E66"),sQuery(id+"F0.wireOp",EDGE,"E67"),sQuery(id+"F0.wireOp",EDGE,"E68"),sQuery(id+"F0.wireOp",EDGE,"E69"),sQuery(id+"F0.wireOp",EDGE,"E70"),sQuery(id+"F0.wireOp",EDGE,"E71"),sQuery(id+"F0.wireOp",EDGE,"E72"),sQuery(id+"F0.wireOp",EDGE,"E73"),sQuery(id+"F0.wireOp",EDGE,"E74"),sQuery(id+"F0.wireOp",EDGE,"E75"),sQuery(id+"F0.wireOp",EDGE,"E76"),sQuery(id+"F0.wireOp",EDGE,"E77"),sQuery(id+"F0.wireOp",EDGE,"E78"),sQuery(id+"F0.wireOp",EDGE,"E79"),sQuery(id+"F0.wireOp",EDGE,"E80"),sQuery(id+"F0.wireOp",EDGE,"E81"),sQuery(id+"F0.wireOp",EDGE,"E82"),sQuery(id+"F0.wireOp",EDGE,"E83"),sQuery(id+"F0.wireOp",EDGE,"E84"),sQuery(id+"F0.wireOp",EDGE,"E85"),sQuery(id+"F0.wireOp",EDGE,"E86"),sQuery(id+"F0.wireOp",EDGE,"E87"),sQuery(id+"F0.wireOp",EDGE,"E88"),sQuery(id+"F0.wireOp",EDGE,"E89"),sQuery(id+"F0.wireOp",EDGE,"E90"),sQuery(id+"F0.wireOp",EDGE,"E91"),sQuery(id+"F0.wireOp",EDGE,"E92"),sQuery(id+"F0.wireOp",EDGE,"E93"),sQuery(id+"F0.wireOp",EDGE,"E94"),sQuery(id+"F0.wireOp",EDGE,"E95"),sQuery(id+"F0.wireOp",EDGE,"E96"),sQuery(id+"F0.wireOp",EDGE,"E97"),sQuery(id+"F0.wireOp",EDGE,"E98"),sQuery(id+"F0.wireOp",EDGE,"E99"),sQuery(id+"F0.wireOp",EDGE,"E100"),sQuery(id+"F0.wireOp",EDGE,"E101"),sQuery(id+"F0.wireOp",EDGE,"E102"),sQuery(id+"F0.wireOp",EDGE,"E103"),sQuery(id+"F0.wireOp",EDGE,"E104"),sQuery(id+"F0.wireOp",EDGE,"E105"),sQuery(id+"F0.wireOp",EDGE,"E106"),sQuery(id+"F0.wireOp",EDGE,"E107"),sQuery(id+"F0.wireOp",EDGE,"E108"),sQuery(id+"F0.wireOp",EDGE,"E109"),sQuery(id+"F0.wireOp",EDGE,"E110"),sQuery(id+"F0.wireOp",EDGE,"E111"),sQuery(id+"F0.wireOp",EDGE,"E112"),sQuery(id+"F0.wireOp",EDGE,"E113"),sQuery(id+"F0.wireOp",EDGE,"E114"),sQuery(id+"F0.wireOp",EDGE,"E115"),sQuery(id+"F0.wireOp",EDGE,"E116"),sQuery(id+"F0.wireOp",EDGE,"E117"),sQuery(id+"F0.wireOp",EDGE,"E118"),sQuery(id+"F0.wireOp",EDGE,"E119"),sQuery(id+"F0.wireOp",EDGE,"E120"),sQuery(id+"F0.wireOp",EDGE,"E121"),sQuery(id+"F0.wireOp",EDGE,"E122"),sQuery(id+"F0.wireOp",EDGE,"E123"),sQuery(id+"F0.wireOp",EDGE,"E124"),sQuery(id+"F0.wireOp",EDGE,"E125"),sQuery(id+"F0.wireOp",EDGE,"E126"),sQuery(id+"F0.wireOp",EDGE,"E127"),sQuery(id+"F0.wireOp",EDGE,"E128"),sQuery(id+"F0.wireOp",EDGE,"E129"),sQuery(id+"F0.wireOp",EDGE,"E130"),sQuery(id+"F0.wireOp",EDGE,"E131"),sQuery(id+"F0.wireOp",EDGE,"E132"),sQuery(id+"F0.wireOp",EDGE,"E133"),sQuery(id+"F0.wireOp",EDGE,"E134"),sQuery(id+"F0.wireOp",EDGE,"E135"),sQuery(id+"F0.wireOp",EDGE,"E136"),sQuery(id+"F0.wireOp",EDGE,"E137"),sQuery(id+"F0.wireOp",EDGE,"E138"),sQuery(id+"F0.wireOp",EDGE,"E139"),sQuery(id+"F0.wireOp",EDGE,"E140"),sQuery(id+"F0.wireOp",EDGE,"E141"),sQuery(id+"F0.wireOp",EDGE,"E142"),sQuery(id+"F0.wireOp",EDGE,"E143"),sQuery(id+"F0.wireOp",EDGE,"E144"),sQuery(id+"F0.wireOp",EDGE,"E145"),sQuery(id+"F0.wireOp",EDGE,"E146"),sQuery(id+"F0.wireOp",EDGE,"E147"),sQuery(id+"F0.wireOp",EDGE,"E148"),sQuery(id+"F0.wireOp",EDGE,"E149"),sQuery(id+"F0.wireOp",EDGE,"E150"),sQuery(id+"F0.wireOp",EDGE,"E151"),sQuery(id+"F0.wireOp",EDGE,"E152"),sQuery(id+"F0.wireOp",EDGE,"E153"),sQuery(id+"F0.wireOp",EDGE,"E154"),sQuery(id+"F0.wireOp",EDGE,"E155"),sQuery(id+"F0.wireOp",EDGE,"E156"),sQuery(id+"F0.wireOp",EDGE,"E157"),sQuery(id+"F0.wireOp",EDGE,"E158"),sQuery(id+"F0.wireOp",EDGE,"E159"),sQuery(id+"F0.wireOp",EDGE,"E160"),sQuery(id+"F0.wireOp",EDGE,"E161"),sQuery(id+"F0.wireOp",EDGE,"E162"),sQuery(id+"F0.wireOp",EDGE,"E163"),sQuery(id+"F0.wireOp",EDGE,"E164"),sQuery(id+"F0.wireOp",EDGE,"E165"),sQuery(id+"F0.wireOp",EDGE,"E166"),sQuery(id+"F0.wireOp",EDGE,"E167"),sQuery(id+"F0.wireOp",EDGE,"E168"),sQuery(id+"F0.wireOp",EDGE,"E169"),sQuery(id+"F0.wireOp",EDGE,"E170"),sQuery(id+"F0.wireOp",EDGE,"E171"),sQuery(id+"F0.wireOp",EDGE,"E172"),sQuery(id+"F0.wireOp",EDGE,"E173"),sQuery(id+"F0.wireOp",EDGE,"E174"),sQuery(id+"F0.wireOp",EDGE,"E175"),sQuery(id+"F0.wireOp",EDGE,"E176"),sQuery(id+"F0.wireOp",EDGE,"E177"),sQuery(id+"F0.wireOp",EDGE,"E178"),sQuery(id+"F0.wireOp",EDGE,"E179"),sQuery(id+"F0.wireOp",EDGE,"E180"),sQuery(id+"F0.wireOp",EDGE,"E181")])],"isStart":true}),makeQuery(id+"F5.opExtrude","SWEPT_FACE",FACE,{"disambiguationData":[OSD([sQuery(id+"F4.wireOp",EDGE,"E189.top")])]}),makeQuery(id+"F5.opExtrude","SWEPT_FACE",FACE,{"disambiguationData":[OSD([sQuery(id+"F4.wireOp",EDGE,"E192.0.3")])]})]}),makeQuery(id+"F7.opExtrude","SWEPT_FACE",FACE,{"disambiguationData":[OSD([sQuery(id+"F6.wireOp",EDGE,"E193.bottom")])]})]});
            var sketch = newSketch(context, id + "F8", { "sketchPlane" : qUnion([Q0])});
            skCircle(sketch, "E194", {"center": v(13.09, 6.92) * mm, "radius": 1.5 * mm});
            skPoint(sketch, "E195", {"position": v(15.59, 6.92) * mm});
            skPoint(sketch, "E196", {"position": v(13.09, 4.42) * mm});
            skSolve(sketch);
        }
        {
            var Q0;
            Q0 = qSketchRegion(id + "F8", true);
            extrude(context, id + "F9", {"entities" : qUnion([Q0]), "operationType" : NewBodyOperationType.REMOVE, "endBound" : BoundingType.UP_TO_NEXT, "oppositeDirection" : true, "depth" : 25 * mm});
        }
        {
            var Q0;
            Q0=qCreatedBy(makeId("Top.planeOp"),FACE);
            var sketch = newSketch(context, id + "F10", { "sketchPlane" : qUnion([Q0])});
            skLineSegment(sketch, "E197.0", {"start": v(-10.25, -9.42) * mm, "end": v(-10.25, -1.42) * mm, "construction": true});
            skLineSegment(sketch, "E198.bottom", {"start": v(-10.25, -9.42) * mm, "end": v(-15.25, -9.42) * mm});
            skLineSegment(sketch, "E198.top", {"start": v(-10.25, -4.42) * mm, "end": v(-15.25, -4.42) * mm});
            skLineSegment(sketch, "E198.left", {"start": v(-10.25, -9.42) * mm, "end": v(-10.25, -4.42) * mm});
            skLineSegment(sketch, "E198.right", {"start": v(-15.25, -9.42) * mm, "end": v(-15.25, -4.42) * mm});
            skCircle(sketch, "E199", {"center": v(-12.75, -6.92) * mm, "radius": 1.5 * mm});
            skPoint(sketch, "E199.centerSnap0", {"position": v(-12.75, -9.42) * mm});
            skPoint(sketch, "E199.centerSnap1", {"position": v(-10.25, -6.92) * mm});
            skSolve(sketch);
        }
        {
            var Q0;
            Q0 = qSketchRegion(id + "F10", true);
            extrude(context, id + "F11", {"entities" : qUnion([Q0]), "operationType" : NewBodyOperationType.ADD, "depth" : 1.5 * mm});
        }
        {
            var Q0;
            Q0=makeQuery(id+"F11.boolean.opBoolean","MERGE",FACE,{"derivedFrom":[makeQuery(id+"F7.boolean.opBoolean","MERGE",FACE,{"derivedFrom":[makeQuery(id+"F5.boolean.opBoolean","MERGE",FACE,{"derivedFrom":[makeQuery(id+"F1.opExtrude","CAP_FACE",FACE,{"disambiguationData":[OSD([sQuery(id+"F0.wireOp",EDGE,"E0"),sQuery(id+"F0.wireOp",EDGE,"E1"),sQuery(id+"F0.wireOp",EDGE,"E2"),sQuery(id+"F0.wireOp",EDGE,"E3"),sQuery(id+"F0.wireOp",EDGE,"E4"),sQuery(id+"F0.wireOp",EDGE,"E5"),sQuery(id+"F0.wireOp",EDGE,"E6"),sQuery(id+"F0.wireOp",EDGE,"E7"),sQuery(id+"F0.wireOp",EDGE,"E8"),sQuery(id+"F0.wireOp",EDGE,"E9"),sQuery(id+"F0.wireOp",EDGE,"E10"),sQuery(id+"F0.wireOp",EDGE,"E11"),sQuery(id+"F0.wireOp",EDGE,"E12"),sQuery(id+"F0.wireOp",EDGE,"E13"),sQuery(id+"F0.wireOp",EDGE,"E14"),sQuery(id+"F0.wireOp",EDGE,"E15"),sQuery(id+"F0.wireOp",EDGE,"E16"),sQuery(id+"F0.wireOp",EDGE,"E17"),sQuery(id+"F0.wireOp",EDGE,"E18"),sQuery(id+"F0.wireOp",EDGE,"E19"),sQuery(id+"F0.wireOp",EDGE,"E20"),sQuery(id+"F0.wireOp",EDGE,"E21"),sQuery(id+"F0.wireOp",EDGE,"E22"),sQuery(id+"F0.wireOp",EDGE,"E23"),sQuery(id+"F0.wireOp",EDGE,"E24"),sQuery(id+"F0.wireOp",EDGE,"E25"),sQuery(id+"F0.wireOp",EDGE,"E26"),sQuery(id+"F0.wireOp",EDGE,"E27"),sQuery(id+"F0.wireOp",EDGE,"E28"),sQuery(id+"F0.wireOp",EDGE,"E29"),sQuery(id+"F0.wireOp",EDGE,"E30"),sQuery(id+"F0.wireOp",EDGE,"E31"),sQuery(id+"F0.wireOp",EDGE,"E32"),sQuery(id+"F0.wireOp",EDGE,"E33"),sQuery(id+"F0.wireOp",EDGE,"E34"),sQuery(id+"F0.wireOp",EDGE,"E35"),sQuery(id+"F0.wireOp",EDGE,"E36"),sQuery(id+"F0.wireOp",EDGE,"E37"),sQuery(id+"F0.wireOp",EDGE,"E38"),sQuery(id+"F0.wireOp",EDGE,"E39"),sQuery(id+"F0.wireOp",EDGE,"E40"),sQuery(id+"F0.wireOp",EDGE,"E41"),sQuery(id+"F0.wireOp",EDGE,"E42"),sQuery(id+"F0.wireOp",EDGE,"E43"),sQuery(id+"F0.wireOp",EDGE,"E44"),sQuery(id+"F0.wireOp",EDGE,"E45"),sQuery(id+"F0.wireOp",EDGE,"E46"),sQuery(id+"F0.wireOp",EDGE,"E47"),sQuery(id+"F0.wireOp",EDGE,"E48"),sQuery(id+"F0.wireOp",EDGE,"E49"),sQuery(id+"F0.wireOp",EDGE,"E50"),sQuery(id+"F0.wireOp",EDGE,"E51"),sQuery(id+"F0.wireOp",EDGE,"E52"),sQuery(id+"F0.wireOp",EDGE,"E53"),sQuery(id+"F0.wireOp",EDGE,"E54"),sQuery(id+"F0.wireOp",EDGE,"E55"),sQuery(id+"F0.wireOp",EDGE,"E56"),sQuery(id+"F0.wireOp",EDGE,"E57"),sQuery(id+"F0.wireOp",EDGE,"E58"),sQuery(id+"F0.wireOp",EDGE,"E59"),sQuery(id+"F0.wireOp",EDGE,"E60"),sQuery(id+"F0.wireOp",EDGE,"E61"),sQuery(id+"F0.wireOp",EDGE,"E62"),sQuery(id+"F0.wireOp",EDGE,"E63"),sQuery(id+"F0.wireOp",EDGE,"E64"),sQuery(id+"F0.wireOp",EDGE,"E65"),sQuery(id+"F0.wireOp",EDGE,"E66"),sQuery(id+"F0.wireOp",EDGE,"E67"),sQuery(id+"F0.wireOp",EDGE,"E68"),sQuery(id+"F0.wireOp",EDGE,"E69"),sQuery(id+"F0.wireOp",EDGE,"E70"),sQuery(id+"F0.wireOp",EDGE,"E71"),sQuery(id+"F0.wireOp",EDGE,"E72"),sQuery(id+"F0.wireOp",EDGE,"E73"),sQuery(id+"F0.wireOp",EDGE,"E74"),sQuery(id+"F0.wireOp",EDGE,"E75"),sQuery(id+"F0.wireOp",EDGE,"E76"),sQuery(id+"F0.wireOp",EDGE,"E77"),sQuery(id+"F0.wireOp",EDGE,"E78"),sQuery(id+"F0.wireOp",EDGE,"E79"),sQuery(id+"F0.wireOp",EDGE,"E80"),sQuery(id+"F0.wireOp",EDGE,"E81"),sQuery(id+"F0.wireOp",EDGE,"E82"),sQuery(id+"F0.wireOp",EDGE,"E83"),sQuery(id+"F0.wireOp",EDGE,"E84"),sQuery(id+"F0.wireOp",EDGE,"E85"),sQuery(id+"F0.wireOp",EDGE,"E86"),sQuery(id+"F0.wireOp",EDGE,"E87"),sQuery(id+"F0.wireOp",EDGE,"E88"),sQuery(id+"F0.wireOp",EDGE,"E89"),sQuery(id+"F0.wireOp",EDGE,"E90"),sQuery(id+"F0.wireOp",EDGE,"E91"),sQuery(id+"F0.wireOp",EDGE,"E92"),sQuery(id+"F0.wireOp",EDGE,"E93"),sQuery(id+"F0.wireOp",EDGE,"E94"),sQuery(id+"F0.wireOp",EDGE,"E95"),sQuery(id+"F0.wireOp",EDGE,"E96"),sQuery(id+"F0.wireOp",EDGE,"E97"),sQuery(id+"F0.wireOp",EDGE,"E98"),sQuery(id+"F0.wireOp",EDGE,"E99"),sQuery(id+"F0.wireOp",EDGE,"E100"),sQuery(id+"F0.wireOp",EDGE,"E101"),sQuery(id+"F0.wireOp",EDGE,"E102"),sQuery(id+"F0.wireOp",EDGE,"E103"),sQuery(id+"F0.wireOp",EDGE,"E104"),sQuery(id+"F0.wireOp",EDGE,"E105"),sQuery(id+"F0.wireOp",EDGE,"E106"),sQuery(id+"F0.wireOp",EDGE,"E107"),sQuery(id+"F0.wireOp",EDGE,"E108"),sQuery(id+"F0.wireOp",EDGE,"E109"),sQuery(id+"F0.wireOp",EDGE,"E110"),sQuery(id+"F0.wireOp",EDGE,"E111"),sQuery(id+"F0.wireOp",EDGE,"E112"),sQuery(id+"F0.wireOp",EDGE,"E113"),sQuery(id+"F0.wireOp",EDGE,"E114"),sQuery(id+"F0.wireOp",EDGE,"E115"),sQuery(id+"F0.wireOp",EDGE,"E116"),sQuery(id+"F0.wireOp",EDGE,"E117"),sQuery(id+"F0.wireOp",EDGE,"E118"),sQuery(id+"F0.wireOp",EDGE,"E119"),sQuery(id+"F0.wireOp",EDGE,"E120"),sQuery(id+"F0.wireOp",EDGE,"E121"),sQuery(id+"F0.wireOp",EDGE,"E122"),sQuery(id+"F0.wireOp",EDGE,"E123"),sQuery(id+"F0.wireOp",EDGE,"E124"),sQuery(id+"F0.wireOp",EDGE,"E125"),sQuery(id+"F0.wireOp",EDGE,"E126"),sQuery(id+"F0.wireOp",EDGE,"E127"),sQuery(id+"F0.wireOp",EDGE,"E128"),sQuery(id+"F0.wireOp",EDGE,"E129"),sQuery(id+"F0.wireOp",EDGE,"E130"),sQuery(id+"F0.wireOp",EDGE,"E131"),sQuery(id+"F0.wireOp",EDGE,"E132"),sQuery(id+"F0.wireOp",EDGE,"E133"),sQuery(id+"F0.wireOp",EDGE,"E134"),sQuery(id+"F0.wireOp",EDGE,"E135"),sQuery(id+"F0.wireOp",EDGE,"E136"),sQuery(id+"F0.wireOp",EDGE,"E137"),sQuery(id+"F0.wireOp",EDGE,"E138"),sQuery(id+"F0.wireOp",EDGE,"E139"),sQuery(id+"F0.wireOp",EDGE,"E140"),sQuery(id+"F0.wireOp",EDGE,"E141"),sQuery(id+"F0.wireOp",EDGE,"E142"),sQuery(id+"F0.wireOp",EDGE,"E143"),sQuery(id+"F0.wireOp",EDGE,"E144"),sQuery(id+"F0.wireOp",EDGE,"E145"),sQuery(id+"F0.wireOp",EDGE,"E146"),sQuery(id+"F0.wireOp",EDGE,"E147"),sQuery(id+"F0.wireOp",EDGE,"E148"),sQuery(id+"F0.wireOp",EDGE,"E149"),sQuery(id+"F0.wireOp",EDGE,"E150"),sQuery(id+"F0.wireOp",EDGE,"E151"),sQuery(id+"F0.wireOp",EDGE,"E152"),sQuery(id+"F0.wireOp",EDGE,"E153"),sQuery(id+"F0.wireOp",EDGE,"E154"),sQuery(id+"F0.wireOp",EDGE,"E155"),sQuery(id+"F0.wireOp",EDGE,"E156"),sQuery(id+"F0.wireOp",EDGE,"E157"),sQuery(id+"F0.wireOp",EDGE,"E158"),sQuery(id+"F0.wireOp",EDGE,"E159"),sQuery(id+"F0.wireOp",EDGE,"E160"),sQuery(id+"F0.wireOp",EDGE,"E161"),sQuery(id+"F0.wireOp",EDGE,"E162"),sQuery(id+"F0.wireOp",EDGE,"E163"),sQuery(id+"F0.wireOp",EDGE,"E164"),sQuery(id+"F0.wireOp",EDGE,"E165"),sQuery(id+"F0.wireOp",EDGE,"E166"),sQuery(id+"F0.wireOp",EDGE,"E167"),sQuery(id+"F0.wireOp",EDGE,"E168"),sQuery(id+"F0.wireOp",EDGE,"E169"),sQuery(id+"F0.wireOp",EDGE,"E170"),sQuery(id+"F0.wireOp",EDGE,"E171"),sQuery(id+"F0.wireOp",EDGE,"E172"),sQuery(id+"F0.wireOp",EDGE,"E173"),sQuery(id+"F0.wireOp",EDGE,"E174"),sQuery(id+"F0.wireOp",EDGE,"E175"),sQuery(id+"F0.wireOp",EDGE,"E176"),sQuery(id+"F0.wireOp",EDGE,"E177"),sQuery(id+"F0.wireOp",EDGE,"E178"),sQuery(id+"F0.wireOp",EDGE,"E179"),sQuery(id+"F0.wireOp",EDGE,"E180"),sQuery(id+"F0.wireOp",EDGE,"E181")])],"isStart":false}),makeQuery(id+"F5.opExtrude","SWEPT_FACE",FACE,{"disambiguationData":[OSD([sQuery(id+"F4.wireOp",EDGE,"E189.bottom")])]}),makeQuery(id+"F5.opExtrude","SWEPT_FACE",FACE,{"disambiguationData":[OSD([sQuery(id+"F4.wireOp",EDGE,"E192.0.1")])]})]}),makeQuery(id+"F7.opExtrude","SWEPT_FACE",FACE,{"disambiguationData":[OSD([sQuery(id+"F6.wireOp",EDGE,"E193.top")])]})]}),makeQuery(id+"F11.opExtrude","CAP_FACE",FACE,{"disambiguationData":[OSD([sQuery(id+"F10.wireOp",EDGE,"E198.bottom"),sQuery(id+"F10.wireOp",EDGE,"E198.top"),sQuery(id+"F10.wireOp",EDGE,"E198.left"),sQuery(id+"F10.wireOp",EDGE,"E198.right"),sQuery(id+"F10.wireOp",EDGE,"E199")])],"isStart":false})]});
            var sketch = newSketch(context, id + "F12", { "sketchPlane" : qUnion([Q0])});
            skLineSegment(sketch, "E200.bottom", {"start": v(-4.8, -7) * mm, "end": v(4.8, -7) * mm});
            skLineSegment(sketch, "E200.top", {"start": v(-9.8, -22.7) * mm, "end": v(9.8, -22.7) * mm});
            skLineSegment(sketch, "E200.left", {"start": v(-9.8, -12) * mm, "end": v(-9.8, -22.7) * mm});
            skLineSegment(sketch, "E200.right", {"start": v(9.8, -12) * mm, "end": v(9.8, -22.7) * mm});
            skPoint(sketch, "E200.middle", {"position": v(0, -14.85) * mm});
            skPoint(sketch, "E201.visualSharp", {"position": v(-9.8, -7) * mm});
            skArc(sketch, "E201.filletArc", {"start": v(-4.8, -7) * mm, "mid": v(-8.34, -8.46) * mm, "end": v(-9.8, -12) * mm});
            skPoint(sketch, "E202.visualSharp", {"position": v(9.8, -7) * mm});
            skArc(sketch, "E202.filletArc", {"start": v(9.8, -12) * mm, "mid": v(8.34, -8.46) * mm, "end": v(4.8, -7) * mm});
            skLineSegment(sketch, "E203", {"start": v(-9.08, -9.42) * mm, "end": v(9.08, -9.42) * mm});
            skSolve(sketch);
        }
        {
            var Q0;
            {var subQ0=sQuery(id+"F12.wireOp",EDGE,"E201.filletArc");var subQ1=sQuery(id+"F12.wireOp",EDGE,"E200.bottom");var subQ2=makeQuery(id+"F12.imprint","INTERSECT",VERTEX,{"derivedFrom":[subQ1,subQ0]});Q0=makeQuery(id+"F12.imprint","IMPRINT",FACE,{"disambiguationData":[TD([[makeQuery(id+"F12.imprint","IMPRINT",EDGE,{"disambiguationData":[TD([[subQ2,-1.0]])],"derivedFrom":subQ1}),-1.0]])]});}
            var Q1;
            {var subQ0=sQuery(id+"F12.wireOp",EDGE,"E202.filletArc");var subQ1=sQuery(id+"F12.wireOp",EDGE,"E200.bottom");var subQ2=makeQuery(id+"F12.imprint","INTERSECT",VERTEX,{"derivedFrom":[subQ1,subQ0]});Q1=makeQuery(id+"F12.imprint","IMPRINT",FACE,{"disambiguationData":[TD([[makeQuery(id+"F12.imprint","IMPRINT",EDGE,{"disambiguationData":[TD([[subQ2,1.0]])],"derivedFrom":subQ1}),-1.0]])]});}
            extrude(context, id + "F13", {"entities" : qUnion([Q0, Q1]), "operationType" : NewBodyOperationType.REMOVE, "endBound" : BoundingType.UP_TO_NEXT, "oppositeDirection" : true, "depth" : 25 * mm});
        }
    });
